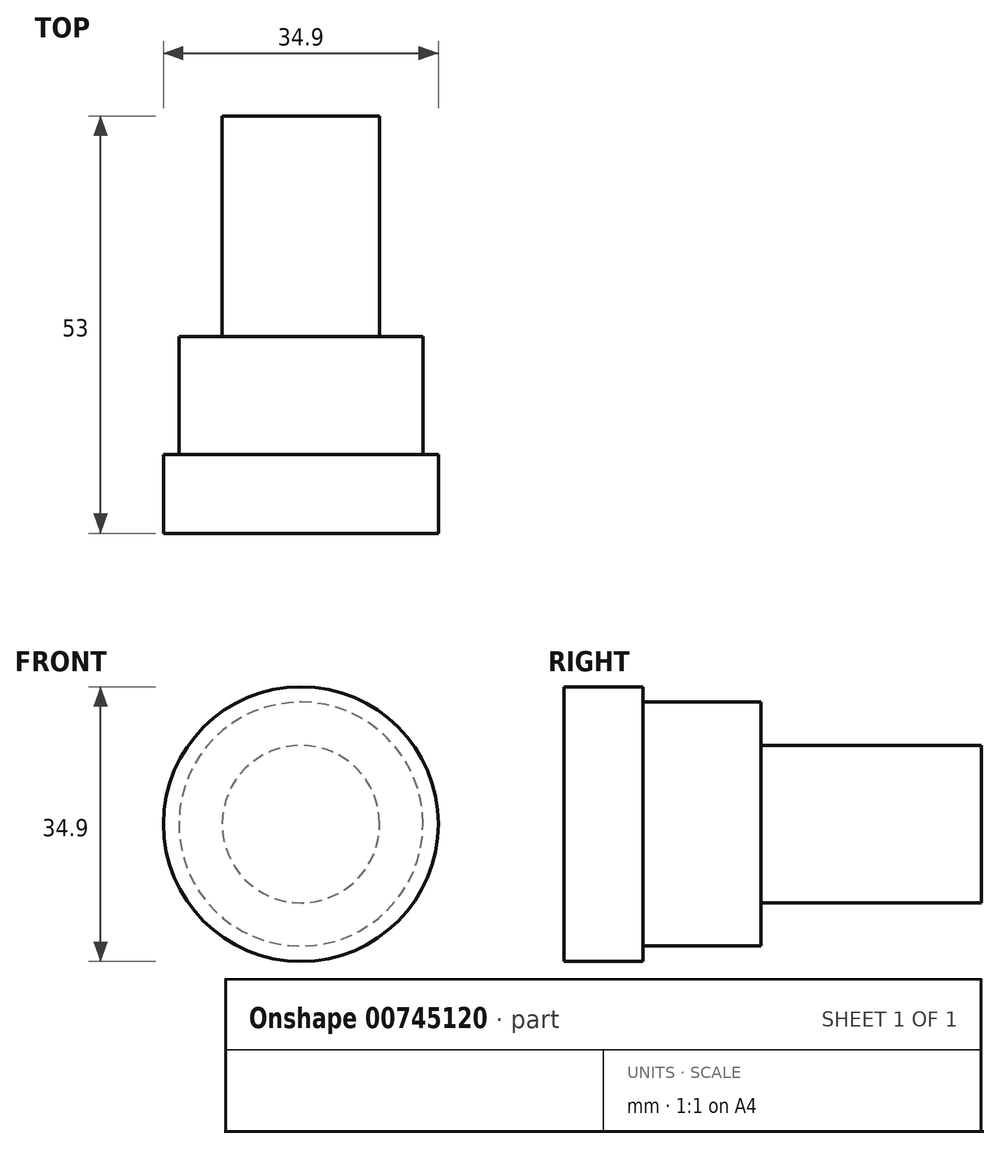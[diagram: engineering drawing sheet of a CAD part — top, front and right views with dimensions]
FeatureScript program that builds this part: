
annotation { "Feature Type Name" : "Feature", "Feature Type Description" : "" }
export const myFeature = defineFeature(function(context is Context, id is Id, definition is map)
    precondition{}
    {
        {
            var Q0;
            Q0=qCreatedBy(makeId("Front.planeOp"),FACE);
            var sketch = newSketch(context, id + "F0", { "sketchPlane" : qUnion([Q0])});
            skCircle(sketch, "E0", {"center": v(0, 0) * mm, "radius": 17.45 * mm});
            skSolve(sketch);
        }
        {
            var Q0;
            Q0 = qSketchRegion(id + "F0", true);
            extrude(context, id + "F1", {"entities" : qUnion([Q0]), "depth" : 25 * mm, "offsetDistance" : 25 * mm});
        }
        {
            var Q0;
            Q0=makeQuery(id+"F1.opExtrude","CAP_FACE",FACE,{"disambiguationData":[OSD([sQuery(id+"F0.wireOp",EDGE,"E0")])],"isStart":true});
            var sketch = newSketch(context, id + "F2", { "sketchPlane" : qUnion([Q0])});
            skCircle(sketch, "E1", {"center": v(0, 0) * mm, "radius": 15.5 * mm});
            skCircle(sketch, "E2", {"center": v(2.9, 0) * mm, "radius": 26.5 * mm});
            skSolve(sketch);
        }
        {
            var Q0;
            Q0 = qSketchRegion(id + "F2", true);
            extrude(context, id + "F3", {"entities" : qUnion([Q0]), "operationType" : NewBodyOperationType.REMOVE, "oppositeDirection" : true, "depth" : 15 * mm, "offsetDistance" : 25 * mm});
        }
        {
            var Q0;
            Q0=makeQuery(id+"F1.opExtrude","CAP_FACE",FACE,{"disambiguationData":[OSD([sQuery(id+"F0.wireOp",EDGE,"E0")])],"isStart":true});
            var sketch = newSketch(context, id + "F4", { "sketchPlane" : qUnion([Q0])});
            skCircle(sketch, "E3", {"center": v(0, 0) * mm, "radius": 10 * mm});
            skSolve(sketch);
        }
        {
            var Q0;
            Q0 = qSketchRegion(id + "F4", true);
            extrude(context, id + "F5", {"entities" : qUnion([Q0]), "operationType" : NewBodyOperationType.ADD, "depth" : 28 * mm, "offsetDistance" : 25 * mm});
        }
    });
